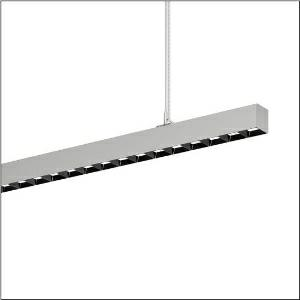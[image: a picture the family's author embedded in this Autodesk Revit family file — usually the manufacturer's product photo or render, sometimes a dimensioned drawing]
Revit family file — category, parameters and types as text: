
# Revit family: silica_r__21_51mx31tctds_9889
name_source: partatom
category: Lighting Fixtures
units: mm (PartAtom-declared; Revit-internal decimal feet)

## family parameters
Cut with Voids When Loaded = No
Host = Face
Light Source = No
Part Type = Normal
Room Calculation Point = No
Round Connector Dimension = Use Diameter
Shared = No

## types (1)
- --- (1 x LED, 15550 lm, 133.9 W, 6500K)
    Apparent Load = 134 VA
    CIE Flux Codes = 85 99 100 60 100
    Color Rendering = 80
    Color Temperature = 6500K
    Default Elevation = 1800 mm
    Description = Silica® 21, office luminaire, primary light control with darklight reflector, of PMMA, black, CAT 2 (L<= 3000cd/m²), light emission: direct/indirect distribution, primary light characteristic: symmetric, installation type: suspended mounting, LED, rated luminous flux: 15.550lm, luminous efficacy: 111lm/W, light colour: 8tw, colour temperature: 2700..6500K, control gear: ECG DALI, with terminal, 3+2-pole, max. 2.5mm², mains connection: 220..240V, AC, 50/60Hz, rated input power: 140.6W, luminaire housing, of aluminium, metallic grey (RAL 9006), length: 3.004mm, width: 53mm, height: 53mm, protection rating (complete): IP20, insulation class (complete): insulation class I (protective earthing), certification: CE, permissible operating ambient temperature: 0..+35°C, standard: EN 50419, packaging unit: 1 piece
    Height = 53 mm
    Lamp = 1 x LED
    Lamp Light Flux = 15550 lm
    Lamp Power = 133.9 W
    Lamp count = 1
    Length = 3004 mm
    Luminous efficacy = 116 lm/W
    Manufacturer = Siteco
    ModVariant = No
    Model = 51MX31TCTDS
    Mounting Place = Ceiling
    Mounting Type = Pendant
    Number of Poles = 1
    OnlyDefault = Yes
    Power Factor = 1
    Product Name = Silica® 21
    Product group = office luminaire | ceiling pendant
    ProductGroupID = 905
    Protection Class = Protection class I
    Protection Degree = IP 20
    RLX_Detail_Level = 1
    RlxData = <blob elided: 62193 chars, md5=96bed371>
    Socket = socket
    Standby Power = 0 W
    System Light Flux = 15550 lm
    System Power = 134 W
    Type Comments = individual setting
    Type Image = l_1251731.jpg
    URL = http://relux.com
    VarID = @adj_045951
    Voltage = 0 V
    Weight = 0.00 kg
    Width = 53 mm

## geometry (parser evidence)
native form markers: Blend x4, Sweep x12
no freeform markers — native parametric forms only
